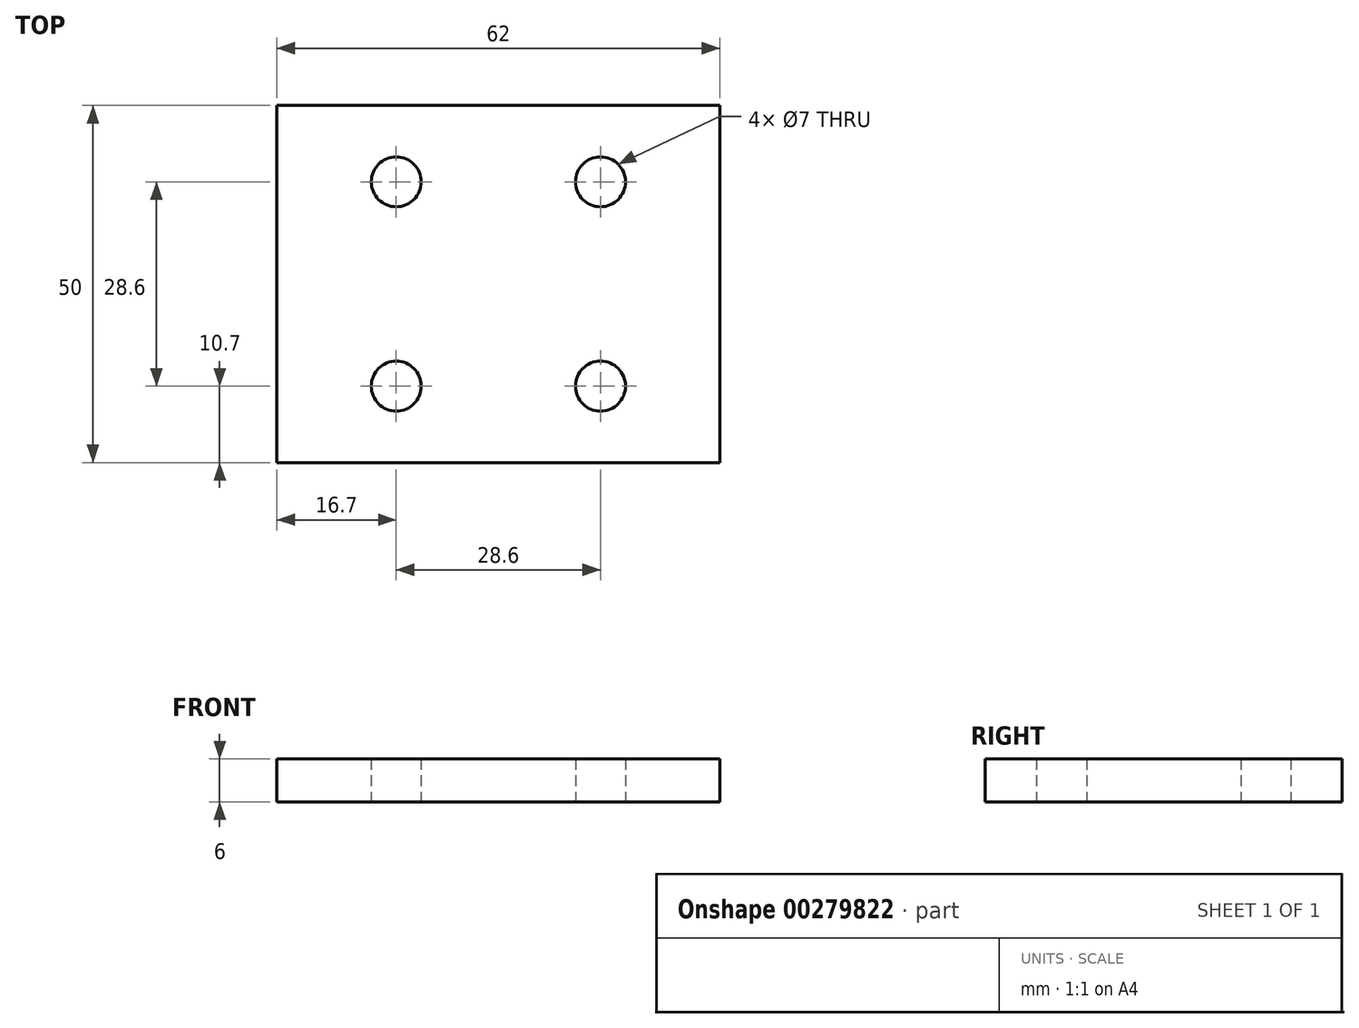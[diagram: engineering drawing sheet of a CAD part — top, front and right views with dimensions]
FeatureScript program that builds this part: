
annotation { "Feature Type Name" : "Feature", "Feature Type Description" : "" }
export const myFeature = defineFeature(function(context is Context, id is Id, definition is map)
    precondition{}
    {
        {
            var Q0;
            Q0=qCreatedBy(makeId("Top.planeOp"),FACE);
            var sketch = newSketch(context, id + "F0", { "sketchPlane" : qUnion([Q0])});
            skLineSegment(sketch, "E0.bottom", {"start": v(0, 0) * mm, "end": v(62, 0) * mm});
            skLineSegment(sketch, "E0.top", {"start": v(0, 50) * mm, "end": v(62, 50) * mm});
            skLineSegment(sketch, "E0.left", {"start": v(0, 0) * mm, "end": v(0, 50) * mm});
            skLineSegment(sketch, "E0.right", {"start": v(62, 0) * mm, "end": v(62, 50) * mm});
            skCircle(sketch, "E1", {"center": v(16.7, 10.7) * mm, "radius": 3.5 * mm});
            skCircle(sketch, "E2", {"center": v(45.3, 10.7) * mm, "radius": 3.5 * mm});
            skCircle(sketch, "E3", {"center": v(45.3, 39.3) * mm, "radius": 3.5 * mm});
            skCircle(sketch, "E4", {"center": v(16.7, 39.3) * mm, "radius": 3.5 * mm});
            skLineSegment(sketch, "E5", {"start": v(31, 50) * mm, "end": v(31, 0) * mm, "construction": true});
            skLineSegment(sketch, "E6", {"start": v(31, 0) * mm, "end": v(31, 10.4) * mm});
            skLineSegment(sketch, "E7", {"start": v(16.7, 39.3) * mm, "end": v(45.3, 39.3) * mm, "construction": true});
            skPoint(sketch, "E8", {"position": v(31, 39.3) * mm});
            skLineSegment(sketch, "E9", {"start": v(0, 25) * mm, "end": v(62, 25) * mm, "construction": true});
            skLineSegment(sketch, "E10", {"start": v(45.3, 39.3) * mm, "end": v(45.3, 10.7) * mm, "construction": true});
            skPoint(sketch, "E11", {"position": v(45.3, 25) * mm});
            skSolve(sketch);
        }
        {
            var Q0;
            Q0 = qSketchRegion(id + "F0", true);
            extrude(context, id + "F1", {"entities" : qUnion([Q0]), "depth" : 6 * mm});
        }
    });
